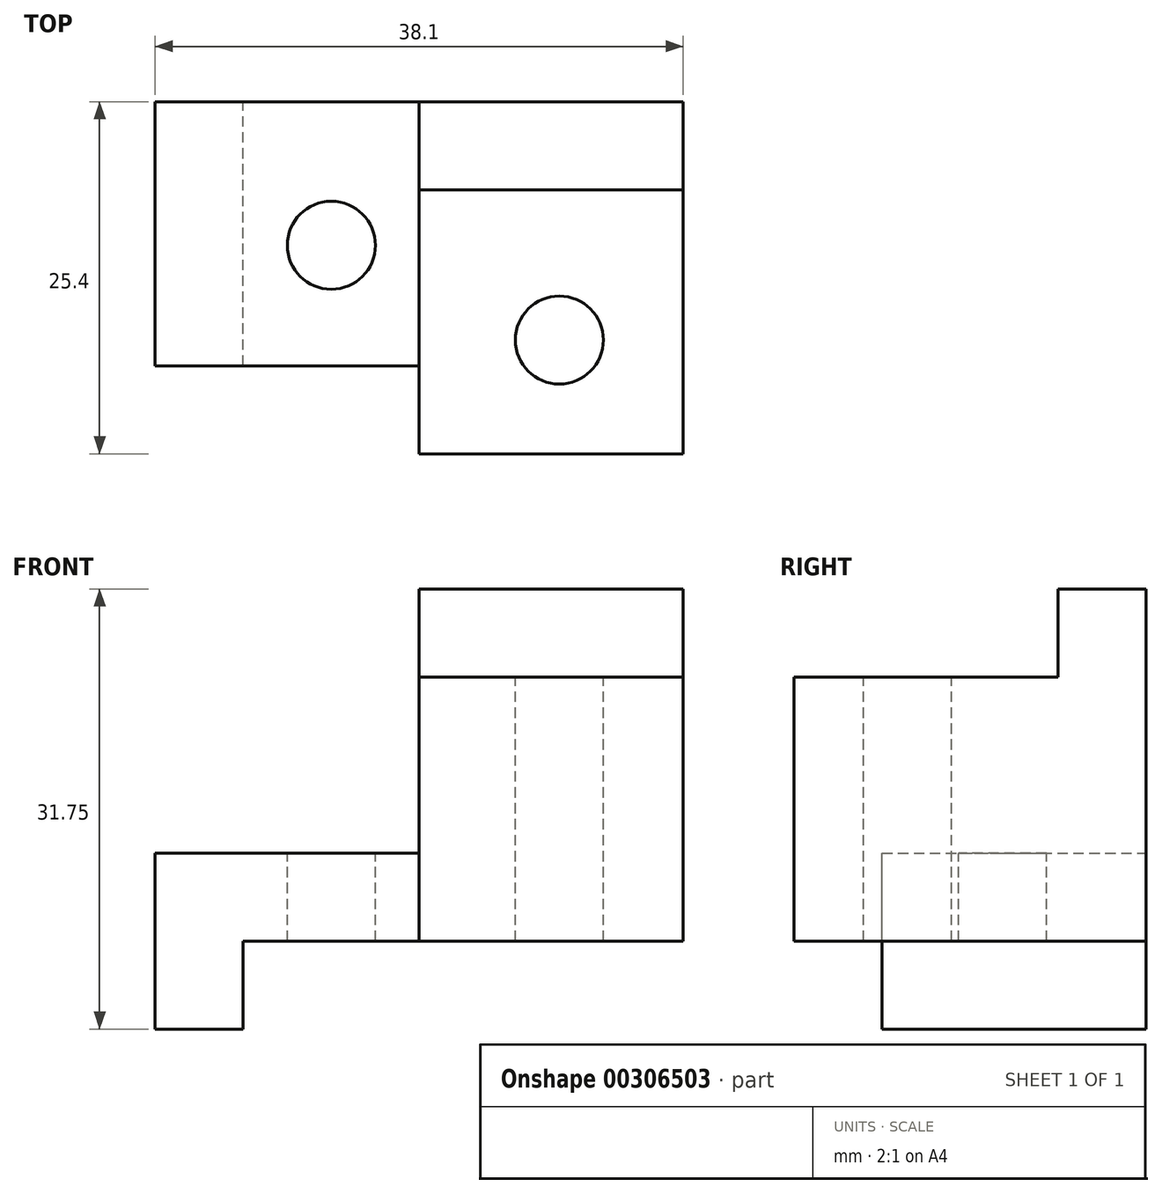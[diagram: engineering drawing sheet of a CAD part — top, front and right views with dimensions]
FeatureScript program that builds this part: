
annotation { "Feature Type Name" : "Feature", "Feature Type Description" : "" }
export const myFeature = defineFeature(function(context is Context, id is Id, definition is map)
    precondition{}
    {
        {
            var Q0;
            Q0=qCreatedBy(makeId("Front.planeOp"),FACE);
            var sketch = newSketch(context, id + "F0", { "sketchPlane" : qUnion([Q0])});
            skLineSegment(sketch, "E0", {"start": v(0, 0) * mm, "end": v(0, 12.7) * mm});
            skLineSegment(sketch, "E1", {"start": v(0, 12.7) * mm, "end": v(19.05, 12.7) * mm});
            skLineSegment(sketch, "E2", {"start": v(19.05, 12.7) * mm, "end": v(19.05, 31.75) * mm});
            skLineSegment(sketch, "E3", {"start": v(19.05, 31.75) * mm, "end": v(38.1, 31.75) * mm});
            skLineSegment(sketch, "E4", {"start": v(38.1, 31.75) * mm, "end": v(38.1, 12.7) * mm});
            skLineSegment(sketch, "E5", {"start": v(38.1, 12.7) * mm, "end": v(38.1, 6.35) * mm});
            skLineSegment(sketch, "E6", {"start": v(38.1, 6.35) * mm, "end": v(6.35, 6.35) * mm});
            skLineSegment(sketch, "E7", {"start": v(6.35, 6.35) * mm, "end": v(6.35, 0) * mm});
            skLineSegment(sketch, "E8", {"start": v(6.35, 0) * mm, "end": v(0, 0) * mm});
            skLineSegment(sketch, "E9", {"start": v(19.05, 25.4) * mm, "end": v(38.1, 25.4) * mm});
            skLineSegment(sketch, "E10", {"start": v(19.05, 12.7) * mm, "end": v(19.05, 6.35) * mm});
            skSolve(sketch);
        }
        {
            var Q0;
            Q0 = qSketchRegion(id + "F0", true);
            extrude(context, id + "F1", {"entities" : qUnion([Q0]), "depth" : 25.4 * mm});
        }
        {
            var Q0;
            Q0=makeQuery(id+"F1.opExtrude","SWEPT_FACE",FACE,{"disambiguationData":[OSD([sQuery(id+"F0.wireOp",EDGE,"E1")])]});
            var sketch = newSketch(context, id + "F2", { "sketchPlane" : qUnion([Q0])});
            skLineSegment(sketch, "E11", {"start": v(19.05, -7.16) * mm, "end": v(38.1, -6.91) * mm});
            skLineSegment(sketch, "E12.bottom", {"start": v(0, -19.05) * mm, "end": v(19.05, -19.05) * mm});
            skLineSegment(sketch, "E12.top", {"start": v(0, -25.4) * mm, "end": v(19.05, -25.4) * mm});
            skLineSegment(sketch, "E12.left", {"start": v(0, -19.05) * mm, "end": v(0, -25.4) * mm});
            skLineSegment(sketch, "E12.right", {"start": v(19.05, -19.05) * mm, "end": v(19.05, -25.4) * mm});
            skSolve(sketch);
        }
        {
            var Q0;
            Q0=makeQuery(id+"F2.imprint","IMPRINT",FACE,{"disambiguationData":[TD([[makeQuery(id+"F2.imprint","IMPRINT",EDGE,{"derivedFrom":sQuery(id+"F2.wireOp",EDGE,"E12.bottom")}),-1.0]])]});
            extrude(context, id + "F3", {"entities" : qUnion([Q0]), "operationType" : NewBodyOperationType.REMOVE, "endBound" : BoundingType.THROUGH_ALL, "oppositeDirection" : true, "depth" : 25.4 * mm});
        }
        {
            var Q0;
            Q0=makeQuery(id+"F1.opExtrude","SWEPT_FACE",FACE,{"disambiguationData":[OSD([sQuery(id+"F0.wireOp",EDGE,"E4"),sQuery(id+"F0.wireOp",EDGE,"E5")])]});
            var sketch = newSketch(context, id + "F4", { "sketchPlane" : qUnion([Q0])});
            skLineSegment(sketch, "E13.bottom", {"start": v(-25.4, 31.75) * mm, "end": v(-6.35, 31.75) * mm});
            skLineSegment(sketch, "E13.top", {"start": v(-25.4, 25.4) * mm, "end": v(-6.35, 25.4) * mm});
            skLineSegment(sketch, "E13.left", {"start": v(-25.4, 31.75) * mm, "end": v(-25.4, 25.4) * mm});
            skLineSegment(sketch, "E13.right", {"start": v(-6.35, 31.75) * mm, "end": v(-6.35, 25.4) * mm});
            skSolve(sketch);
        }
        {
            var Q0;
            Q0 = qSketchRegion(id + "F4", true);
            extrude(context, id + "F5", {"entities" : qUnion([Q0]), "operationType" : NewBodyOperationType.REMOVE, "endBound" : BoundingType.THROUGH_ALL, "oppositeDirection" : true, "depth" : 25.4 * mm});
        }
        {
            var Q0;
            Q0=makeQuery(id+"F1.opExtrude","SWEPT_FACE",FACE,{"disambiguationData":[OSD([sQuery(id+"F0.wireOp",EDGE,"E1")])]});
            var sketch = newSketch(context, id + "F6", { "sketchPlane" : qUnion([Q0])});
            skPoint(sketch, "E14.centerSnap0", {"position": v(9.53, -19.05) * mm});
            skCircle(sketch, "E15", {"center": v(29.16, -17.2) * mm, "radius": 3.18 * mm});
            skCircle(sketch, "E16", {"center": v(12.71, -10.36) * mm, "radius": 3.18 * mm});
            skSolve(sketch);
        }
        {
            var Q0;
            Q0 = qSketchRegion(id + "F6", true);
            extrude(context, id + "F7", {"entities" : qUnion([Q0]), "operationType" : NewBodyOperationType.REMOVE, "endBound" : BoundingType.SYMMETRIC, "oppositeDirection" : true, "depth" : 25.4 * mm});
        }
    });
